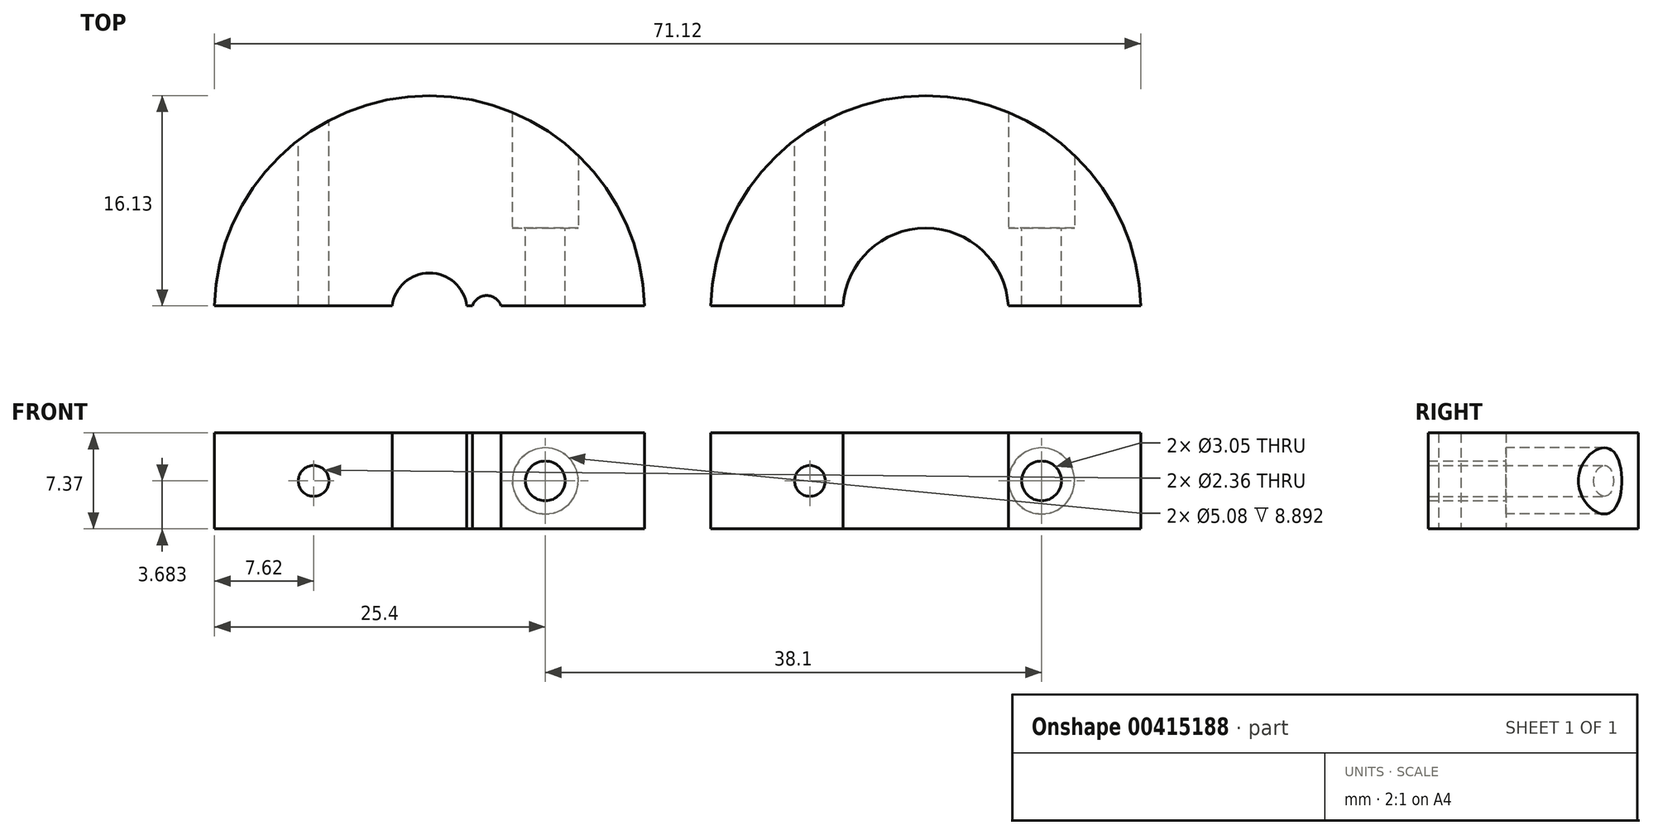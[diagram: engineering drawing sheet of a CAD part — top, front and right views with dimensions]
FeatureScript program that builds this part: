
annotation { "Feature Type Name" : "Feature", "Feature Type Description" : "" }
export const myFeature = defineFeature(function(context is Context, id is Id, definition is map)
    precondition{}
    {
        {
            var Q0;
            Q0=qCreatedBy(makeId("Top.planeOp"),FACE);
            var sketch = newSketch(context, id + "F0", { "sketchPlane" : qUnion([Q0])});
            skCircle(sketch, "E0", {"center": v(-38.1, 0) * mm, "radius": 16.51 * mm});
            skCircle(sketch, "E1", {"center": v(0, 0) * mm, "radius": 16.51 * mm});
            skLineSegment(sketch, "E2", {"start": v(-38.1, 0) * mm, "end": v(0, 0) * mm, "construction": true});
            skCircle(sketch, "E3", {"center": v(-38.1, 0) * mm, "radius": 2.9 * mm});
            skCircle(sketch, "E4", {"center": v(0, 0) * mm, "radius": 6.35 * mm});
            skCircle(sketch, "E5", {"center": v(-33.7, 0) * mm, "radius": 1.17 * mm});
            skSolve(sketch);
        }
        {
            var Q0;
            Q0 = qSketchRegion(id + "F0", true);
            extrude(context, id + "F1", {"entities" : qUnion([Q0]), "depth" : 7.37 * mm});
        }
        {
            var Q0;
            Q0=qCreatedBy(makeId("Top.planeOp"),FACE);
            var sketch = newSketch(context, id + "F2", { "sketchPlane" : qUnion([Q0])});
            skLineSegment(sketch, "E6.bottom", {"start": v(-71.12, 0.38) * mm, "end": v(17.78, 0.38) * mm});
            skLineSegment(sketch, "E6.top", {"start": v(-71.12, -25.4) * mm, "end": v(17.78, -25.4) * mm});
            skLineSegment(sketch, "E6.left", {"start": v(-71.12, 0.38) * mm, "end": v(-71.12, -25.4) * mm});
            skLineSegment(sketch, "E6.right", {"start": v(17.78, 0.38) * mm, "end": v(17.78, -25.4) * mm});
            skSolve(sketch);
        }
        {
            var Q0;
            Q0 = qSketchRegion(id + "F2", true);
            extrude(context, id + "F3", {"entities" : qUnion([Q0]), "operationType" : NewBodyOperationType.REMOVE, "depth" : 25.4 * mm});
        }
        {
            var Q0;
            Q0=qCreatedBy(makeId("Front.planeOp"),FACE);
            cPlane(context, id + "F4", {"entities" : qUnion([Q0]), "cplaneType" : CPlaneType.OFFSET, "offset" : 25.4 * mm, "oppositeDirection" : true, "width" : 152.4 * mm, "height" : 152.4 * mm});
        }
        {
            var Q0;
            Q0=qCreatedBy(id+"F4.planeOp",FACE);
            var sketch = newSketch(context, id + "F5", { "sketchPlane" : qUnion([Q0])});
            skCircle(sketch, "E7", {"center": v(8.9, 3.68) * mm, "radius": 1.52 * mm});
            skCircle(sketch, "E8", {"center": v(-8.9, 3.68) * mm, "radius": 1.18 * mm});
            skCircle(sketch, "E9.1.0.0", {"center": v(-47, 3.68) * mm, "radius": 1.18 * mm});
            skCircle(sketch, "E9.1.0.1", {"center": v(-29.21, 3.68) * mm, "radius": 1.52 * mm});
            skLineSegment(sketch, "E9.direction1", {"start": v(-8.89, 3.68) * mm, "end": v(-47, 3.68) * mm, "construction": true});
            skSolve(sketch);
        }
        {
            var Q0;
            Q0 = qSketchRegion(id + "F5", true);
            extrude(context, id + "F6", {"entities" : qUnion([Q0]), "operationType" : NewBodyOperationType.REMOVE, "depth" : 25.4 * mm});
        }
        {
            var Q0;
            Q0=qCreatedBy(makeId("Front.planeOp"),FACE);
            cPlane(context, id + "F7", {"entities" : qUnion([Q0]), "cplaneType" : CPlaneType.OFFSET, "offset" : 6.35 * mm, "oppositeDirection" : true, "width" : 152.4 * mm, "height" : 152.4 * mm});
        }
        {
            var Q0;
            Q0=qCreatedBy(id+"F7.planeOp",FACE);
            var sketch = newSketch(context, id + "F8", { "sketchPlane" : qUnion([Q0])});
            skCircle(sketch, "E10", {"center": v(8.9, 3.68) * mm, "radius": 2.54 * mm});
            skCircle(sketch, "E11", {"center": v(-29.21, 3.68) * mm, "radius": 2.54 * mm});
            skSolve(sketch);
        }
        {
            var Q0;
            Q0 = qSketchRegion(id + "F8", true);
            extrude(context, id + "F9", {"entities" : qUnion([Q0]), "operationType" : NewBodyOperationType.REMOVE, "oppositeDirection" : true, "depth" : 25.4 * mm});
        }
    });
